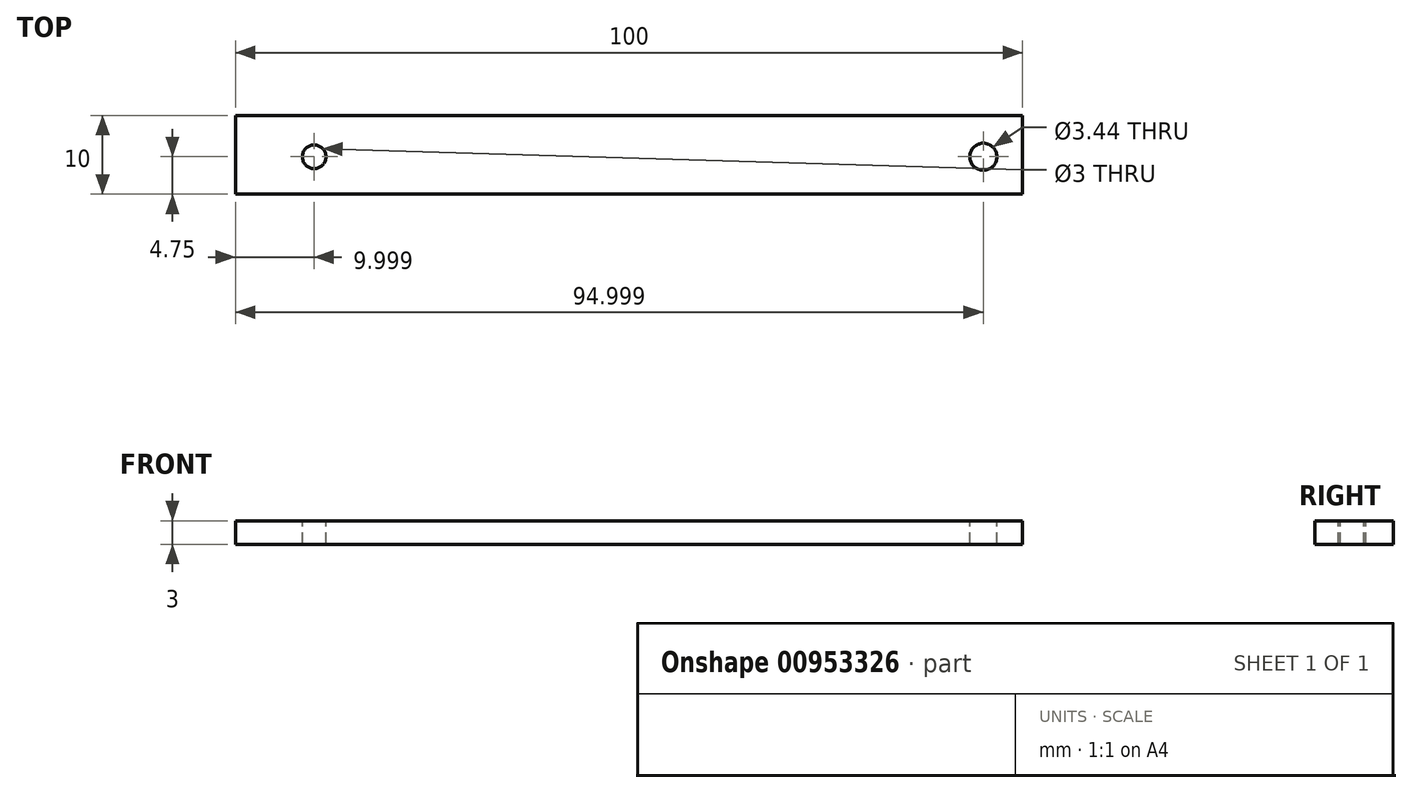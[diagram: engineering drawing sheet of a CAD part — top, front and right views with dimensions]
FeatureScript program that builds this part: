
annotation { "Feature Type Name" : "Feature", "Feature Type Description" : "" }
export const myFeature = defineFeature(function(context is Context, id is Id, definition is map)
    precondition{}
    {
        {
            var Q0;
            Q0=qCreatedBy(makeId("Top.planeOp"),FACE);
            var sketch = newSketch(context, id + "F0", { "sketchPlane" : qUnion([Q0])});
            skLineSegment(sketch, "E0.bottom", {"start": v(50.72, -4.75) * mm, "end": v(-49.28, -4.75) * mm});
            skLineSegment(sketch, "E0.top", {"start": v(50.72, 5.25) * mm, "end": v(-49.28, 5.25) * mm});
            skLineSegment(sketch, "E0.left", {"start": v(50.72, -4.75) * mm, "end": v(50.72, 5.25) * mm});
            skLineSegment(sketch, "E0.right", {"start": v(-49.28, -4.75) * mm, "end": v(-49.28, 5.25) * mm});
            skPoint(sketch, "E0.middle", {"position": v(0.72, 0.25) * mm});
            skSolve(sketch);
        }
        {
            var Q0;
            Q0=makeQuery(id+"F0.imprint","IMPRINT",FACE,{"disambiguationData":[TD([[makeQuery(id+"F0.imprint","IMPRINT",EDGE,{"derivedFrom":sQuery(id+"F0.wireOp",EDGE,"E0.bottom")}),-1.0]])]});
            extrude(context, id + "F1", {"entities" : qUnion([Q0]), "depth" : 3 * mm, "offsetDistance" : 25 * mm});
        }
        {
            var Q0;
            Q0=makeQuery(id+"F1.opExtrude","CAP_FACE",FACE,{"disambiguationData":[OSD([sQuery(id+"F0.wireOp",EDGE,"E0.bottom"),sQuery(id+"F0.wireOp",EDGE,"E0.top"),sQuery(id+"F0.wireOp",EDGE,"E0.left"),sQuery(id+"F0.wireOp",EDGE,"E0.right")])],"isStart":false});
            var sketch = newSketch(context, id + "F2", { "sketchPlane" : qUnion([Q0])});
            skCircle(sketch, "E1", {"center": v(-39.28, 0) * mm, "radius": 1.5 * mm});
            skCircle(sketch, "E2", {"center": v(45.72, 0) * mm, "radius": 1.72 * mm});
            skSolve(sketch);
        }
        {
            var Q0;
            Q0=makeQuery(id+"F2.imprint","IMPRINT",FACE,{"disambiguationData":[TD([[makeQuery(id+"F2.imprint","IMPRINT",EDGE,{"derivedFrom":sQuery(id+"F2.wireOp",EDGE,"E1")}),1.0]])]});
            var Q1;
            Q1=makeQuery(id+"F2.imprint","IMPRINT",FACE,{"disambiguationData":[TD([[makeQuery(id+"F2.imprint","IMPRINT",EDGE,{"derivedFrom":sQuery(id+"F2.wireOp",EDGE,"E2")}),1.0]])]});
            extrude(context, id + "F3", {"entities" : qUnion([Q0, Q1]), "operationType" : NewBodyOperationType.REMOVE, "oppositeDirection" : true, "depth" : 25 * mm, "offsetDistance" : 25 * mm});
        }
    });
